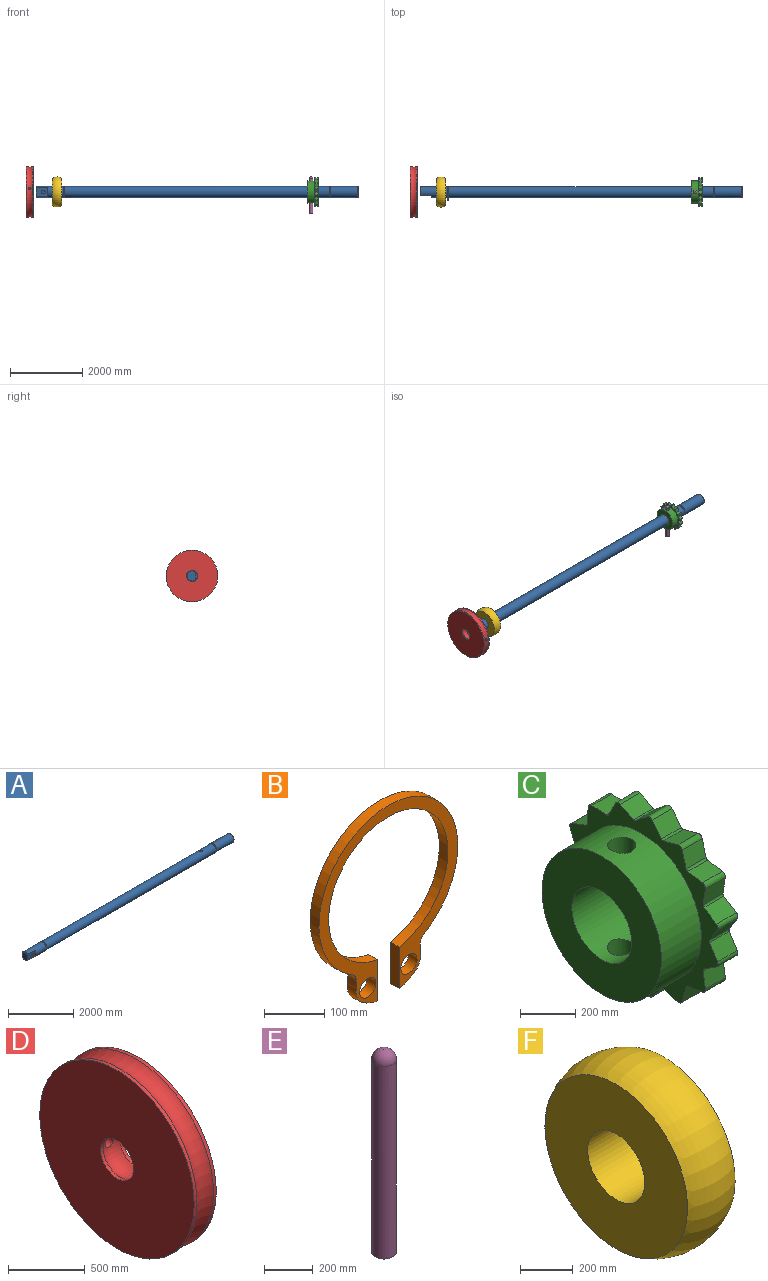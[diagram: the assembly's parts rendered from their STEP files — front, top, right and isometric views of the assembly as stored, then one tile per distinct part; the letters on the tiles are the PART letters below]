
ASSEMBLY  parts=6 mates=6
PART A: 18 faces, bbox 8890x304.8x304.8 mm
  f0: plane 279.4x241.3mm, normal (-1,0,0), area 56290.2mm2, adj f2,f15
  f1: cylinder r=152.4mm len=749.3mm, axis (-1,0,0), area 639360mm2, adj f2,f11,f14,f15
  f2: cone r=139.7mm half-angle=45deg, axis (1,0,0), area 12278.4mm2, adj f0,f1,f15
  f3: plane 279.4x279.4mm, normal (1,0,0), area 61311.6mm2, adj f12
  f4: cylinder r=152.4mm len=749.3mm, axis (-1,0,0), area 717497.8mm2, adj f5,f12
  f5: plane 304.8x304.8mm, normal (-1,0,0), area 31922.6mm2, adj f4,f6
  f6: cylinder r=114.3mm len=228.6mm, axis (-1,0,0), area 18241.5mm2, adj f5,f7
  f7: plane 304.8x304.8mm, normal (1,0,0), area 31922.6mm2, adj f6,f8
  f8: cylinder r=152.4mm len=7315.2mm, axis (-1,0,0), area 6988289.9mm2, adj f7,f9,f13
  f9: plane 304.8x304.8mm, normal (-1,0,0), area 31922.6mm2, adj f8,f10
  f10: cylinder r=114.3mm len=228.6mm, axis (-1,0,0), area 18241.5mm2, adj f9,f11
  f11: plane 304.8x304.8mm, normal (1,0,0), area 31922.6mm2, adj f1,f10
  f12: cone r=152.4mm half-angle=45deg, axis (-1,0,0), area 16481.6mm2, adj f3,f4
  f13: cylinder r=50.8mm len=304.8mm, axis (0,0,1), area 94524.2mm2, adj f8
  f14: plane 227.18x50.8mm, normal (-1,0,0), area 7993.5mm2, adj f1,f15
  f15: plane 317.5x227.19mm, normal (0,-1,0), area 63801.9mm2, adj f0,f1,f2,f14,f16
  f16: cylinder r=50.8mm len=101.6mm, axis (0,1,0), area 8107.3mm2, adj f15,f17
  f17: plane 101.6x101.6mm, normal (0,-1,0), area 8107.3mm2, adj f16
PART B: 16 faces, bbox 325.1x20.3x383.8 mm
  f0: cylinder r=20.32mm len=20.32mm, axis (0,1,0), area 404.6mm2, adj f1,f12,f14,f15
  f1: plane 20.32x12.7mm, normal (-1,0,0), area 258.1mm2, adj f0,f2,f14,f15
  f2: cylinder r=38.1mm len=33.8mm, axis (0,1,0), area 737.9mm2, adj f1,f3,f14,f15
  f3: cylinder r=88.9mm len=40.51mm, axis (0,1,0), area 915mm2, adj f2,f4,f14,f15
  f4: plane 83.82x20.32mm, normal (1,0,0), area 1703.2mm2, adj f3,f5,f14,f15
  f5: cylinder r=139.7mm len=279.4mm, axis (0,1,0), area 16798.1mm2, adj f4,f6,f14,f15
  f6: plane 83.82x20.32mm, normal (-1,0,0), area 1703.2mm2, adj f5,f7,f14,f15
  f7: cylinder r=88.9mm len=40.51mm, axis (0,1,0), area 915mm2, adj f6,f8,f14,f15
  f8: cylinder r=38.1mm len=33.8mm, axis (0,1,0), area 737.9mm2, adj f7,f9,f14,f15
  f9: plane 20.32x12.7mm, normal (1,0,0), area 258.1mm2, adj f8,f10,f14,f15
  f10: cylinder r=20.32mm len=20.32mm, axis (0,1,0), area 404.6mm2, adj f9,f12,f14,f15
  f11: cylinder r=19.05mm len=38.1mm, axis (0,1,0), area 2432.2mm2, adj f14,f15
  f12: cylinder r=162.56mm len=325.12mm, axis (0,1,0), area 17175.7mm2, adj f0,f10,f14,f15
  f13: cylinder r=19.05mm len=38.1mm, axis (0,1,0), area 2432.2mm2, adj f14,f15
  f14: plane 383.75x325.12mm, normal (0,-1,0), area 23940.7mm2, adj f0,f1,f2,f3,f4,f5,f6,f7
  f15: plane 383.75x325.12mm, normal (0,1,0), area 23940.7mm2, adj f0,f1,f2,f3,f4,f5,f6,f7
PART C: 67 faces, bbox 304.8x789.2x793.3 mm
  f0: plane 609.6x609.6mm, normal (-1,0,0), area 218897.6mm2, adj f1,f4
  f1: cylinder r=152.4mm len=304.8mm, axis (-1,0,0), area 275429.2mm2, adj f0,f2,f5,f6
  f2: plane 793.34x789.19mm, normal (1,0,0), area 359950.9mm2, adj f1,f7,f8,f9,f10,f11,f12,f13
  f3: plane 793.34x789.19mm, normal (-1,0,0), area 141053.3mm2, adj f4,f7,f8,f9,f10,f11,f12,f13
  f4: cylinder r=304.8mm len=609.6mm, axis (-1,0,0), area 372930.5mm2, adj f0,f3,f5,f6
  f5: cylinder r=50.8mm len=161.12mm, axis (0,0,1), area 49346.9mm2, adj f1,f4
  f6: cylinder r=50.8mm len=161.12mm, axis (0,0,1), area 49345.3mm2, adj f1,f4
  f7: plane 101.6x73.6mm, normal (0,0.26,0.97), area 7741.9mm2, adj f2,f3,f8,f66
  f8: cylinder r=10.07mm len=101.6mm, axis (1,0,0), area 1178.2mm2, adj f2,f3,f7,f9
  f9: plane 101.6x59.22mm, normal (0,-0.78,0.63), area 7741.9mm2, adj f2,f3,f8,f10
  f10: cylinder r=17.96mm len=101.6mm, axis (1,0,0), area 2866.4mm2, adj f2,f3,f9,f11
  f11: plane 101.6x59.22mm, normal (0,0.63,0.78), area 7741.9mm2, adj f2,f3,f10,f12
  f12: cylinder r=10.07mm len=101.6mm, axis (1,0,0), area 1178.2mm2, adj f2,f3,f11,f13
  f13: plane 101.6x67.89mm, normal (0,-0.45,0.89), area 7741.9mm2, adj f2,f3,f12,f14
  f14: cylinder r=17.96mm len=101.6mm, axis (1,0,0), area 2866.4mm2, adj f2,f3,f13,f15
  f15: plane 101.6x67.89mm, normal (0,0.89,0.45), area 7741.9mm2, adj f2,f3,f14,f16
  f16: cylinder r=10.07mm len=101.6mm, axis (1,0,0), area 1178.2mm2, adj f2,f3,f15,f17
  f17: plane 101.6x76.1mm, normal (0,-0.05,1), area 7741.9mm2, adj f2,f3,f16,f18
  f18: cylinder r=17.96mm len=101.6mm, axis (1,0,0), area 2866.4mm2, adj f2,f3,f17,f19
  f19: plane 101.6x76.1mm, normal (0,1,0.05), area 7741.9mm2, adj f2,f3,f18,f20
  f20: cylinder r=10.07mm len=101.6mm, axis (1,0,0), area 1178.2mm2, adj f2,f3,f19,f21
  f21: plane 101.6x71.14mm, normal (0,0.36,0.93), area 7741.9mm2, adj f2,f3,f20,f22
  f22: cylinder r=17.96mm len=101.6mm, axis (1,0,0), area 2866.4mm2, adj f2,f3,f21,f23
  f23: plane 101.6x71.14mm, normal (0,0.93,-0.36), area 7741.9mm2, adj f2,f3,f22,f24
  f24: cylinder r=10.07mm len=101.6mm, axis (1,0,0), area 1178.2mm2, adj f2,f3,f23,f25
  f25: plane 101.6x53.88mm, normal (0,0.71,0.71), area 7741.9mm2, adj f2,f3,f24,f26
  f26: cylinder r=17.96mm len=101.6mm, axis (1,0,0), area 2866.4mm2, adj f2,f3,f25,f27
  f27: plane 101.6x53.88mm, normal (0,0.71,-0.71), area 7741.9mm2, adj f2,f3,f26,f28
  f28: cylinder r=10.07mm len=101.6mm, axis (1,0,0), area 1178.2mm2, adj f2,f3,f27,f29
  f29: plane 101.6x71.14mm, normal (0,0.93,0.36), area 7741.9mm2, adj f2,f3,f28,f30
  f30: cylinder r=17.96mm len=101.6mm, axis (1,0,0), area 2866.4mm2, adj f2,f3,f29,f31
  f31: plane 101.6x71.14mm, normal (0,0.36,-0.93), area 7741.9mm2, adj f2,f3,f30,f32
  f32: cylinder r=10.07mm len=101.6mm, axis (1,0,0), area 1178.2mm2, adj f2,f3,f31,f33
  f33: plane 101.6x76.1mm, normal (0,1,-0.05), area 7741.9mm2, adj f2,f3,f32,f34
  f34: cylinder r=17.96mm len=101.6mm, axis (1,0,0), area 2866.4mm2, adj f2,f3,f33,f35
  f35: plane 101.6x76.1mm, normal (0,-0.05,-1), area 7741.9mm2, adj f2,f3,f34,f36
  f36: cylinder r=10.07mm len=101.6mm, axis (1,0,0), area 1178.2mm2, adj f2,f3,f35,f37
  f37: plane 101.6x67.89mm, normal (0,0.89,-0.45), area 7741.9mm2, adj f2,f3,f36,f38
  f38: cylinder r=17.96mm len=101.6mm, axis (1,0,0), area 2866.4mm2, adj f2,f3,f37,f39
  f39: plane 101.6x67.89mm, normal (0,-0.45,-0.89), area 7741.9mm2, adj f2,f3,f38,f40
  f40: cylinder r=10.07mm len=101.6mm, axis (1,0,0), area 1178.2mm2, adj f2,f3,f39,f41
  f41: plane 101.6x59.22mm, normal (0,0.63,-0.78), area 7741.9mm2, adj f2,f3,f40,f42
  f42: cylinder r=17.96mm len=101.6mm, axis (1,0,0), area 2866.4mm2, adj f2,f3,f41,f43
  f43: plane 101.6x59.22mm, normal (0,-0.78,-0.63), area 7741.9mm2, adj f2,f3,f42,f44
  f44: cylinder r=10.07mm len=101.6mm, axis (1,0,0), area 1178.2mm2, adj f2,f3,f43,f45
  f45: plane 101.6x73.6mm, normal (0,0.26,-0.97), area 7741.9mm2, adj f2,f3,f44,f46
  f46: cylinder r=17.96mm len=101.6mm, axis (1,0,0), area 2866.4mm2, adj f2,f3,f45,f47
  f47: plane 101.6x73.6mm, normal (0,-0.97,-0.26), area 7741.9mm2, adj f2,f3,f46,f48
  f48: cylinder r=10.07mm len=101.6mm, axis (1,0,0), area 1178.2mm2, adj f2,f3,f47,f49
  f49: plane 101.6x75.26mm, normal (0,-0.16,-0.99), area 7741.9mm2, adj f2,f3,f48,f50
  f50: cylinder r=17.96mm len=101.6mm, axis (1,0,0), area 2866.4mm2, adj f2,f3,f49,f51
  f51: plane 101.6x75.26mm, normal (0,-0.99,0.16), area 7741.9mm2, adj f2,f3,f50,f52
  f52: cylinder r=10.07mm len=101.6mm, axis (1,0,0), area 1178.2mm2, adj f2,f3,f51,f53
  f53: plane 101.6x63.91mm, normal (0,-0.54,-0.84), area 7741.9mm2, adj f2,f3,f52,f54
  f54: cylinder r=17.96mm len=101.6mm, axis (1,0,0), area 2866.4mm2, adj f2,f3,f53,f55
  f55: plane 101.6x63.91mm, normal (0,-0.84,0.54), area 7741.9mm2, adj f2,f3,f54,f56
  f56: cylinder r=10.07mm len=101.6mm, axis (1,0,0), area 1178.2mm2, adj f2,f3,f55,f57
  f57: plane 101.6x63.91mm, normal (0,-0.84,-0.54), area 7741.9mm2, adj f2,f3,f56,f58
  f58: cylinder r=17.96mm len=101.6mm, axis (1,0,0), area 2866.4mm2, adj f2,f3,f57,f59
  f59: plane 101.6x63.91mm, normal (0,-0.54,0.84), area 7741.9mm2, adj f2,f3,f58,f60
  f60: cylinder r=10.07mm len=101.6mm, axis (1,0,0), area 1178.2mm2, adj f2,f3,f59,f61
  f61: plane 101.6x75.26mm, normal (0,-0.99,-0.16), area 7741.9mm2, adj f2,f3,f60,f62
  f62: cylinder r=17.96mm len=101.6mm, axis (1,0,0), area 2866.4mm2, adj f2,f3,f61,f63
  f63: plane 101.6x75.26mm, normal (0,-0.16,0.99), area 7741.9mm2, adj f2,f3,f62,f64
  f64: cylinder r=10.07mm len=101.6mm, axis (1,0,0), area 1178.2mm2, adj f2,f3,f63,f65
  f65: plane 101.6x73.6mm, normal (0,-0.97,0.26), area 7741.9mm2, adj f2,f3,f64,f66
  f66: cylinder r=17.96mm len=101.6mm, axis (1,0,0), area 2866.4mm2, adj f2,f3,f7,f65
PART D: 9 faces, bbox 203.2x1564.3x1564.3 mm
  f0: torus R=50.8mm, axis (-1,0,0), area 169130.2mm2, adj f1,f7,f8
  f1: cylinder r=152.4mm len=304.8mm, axis (-1,0,0), area 24322mm2, adj f0,f2
  f2: plane 1422.4x1422.4mm, normal (1,0,0), area 1516068.8mm2, adj f1,f3
  f3: cylinder r=711.2mm len=1422.4mm, axis (-1,0,0), area 113502.5mm2, adj f2,f4
  f4: torus R=812.8mm, axis (-1,0,0), area 708556.6mm2, adj f3,f5,f8
  f5: cylinder r=711.2mm len=1422.4mm, axis (-1,0,0), area 113502.5mm2, adj f4,f6
  f6: plane 1422.4x1422.4mm, normal (-1,0,0), area 1516068.8mm2, adj f5,f7
  f7: cylinder r=152.4mm len=304.8mm, axis (-1,0,0), area 24322mm2, adj f0,f6
  f8: cylinder r=38.1mm len=519.7mm, axis (0,-1,0), area 123373.9mm2, adj f0,f4
PART E: 3 faces, bbox 101.6x101.6x1016 mm
  f0: cylinder r=50.8mm len=965.2mm, axis (0,0,-1), area 308078.1mm2, adj f1,f2
  f1: plane 101.6x101.6mm, normal (0,0,-1), area 8107.3mm2, adj f0
  f2: sphere r=50.8mm, area 16214.6mm2, adj f0
PART F: 4 faces, bbox 254x762x796 mm
  f0: plane 762x762mm, normal (-1,0,0), area 383070.9mm2, adj f1,f3
  f1: cylinder r=152.4mm len=304.8mm, axis (-1,0,0), area 243219.6mm2, adj f0,f2
  f2: plane 762x762mm, normal (1,0,0), area 383070.9mm2, adj f1,f3
  f3: torus R=161.03mm, axis (-1,0,0), area 674487.1mm2, adj f0,f2
PLACE A at identity fixed
PLACE B rot(axis=(-0.58,0.58,0.58),120deg) t=(-3675.95,0,0)mm
PLACE C t=(3048,0,0)mm
PLACE D rot(axis=(1,0,0),171.8deg) t=(-4620.5,0,0)mm
PLACE E t=(3149.6,0,-591.66)mm
PLACE F rot(axis=(-1,0,0),26.9deg) t=(-3868.57,0,0)mm
MATE slider E.f0 <-> A.f13  axis (0,0,-1) through (3149.6,0,-109.06)mm
MATE cylindrical D.f0 <-> A.f1  axis (-1,0,0) through (-4544.3,0,0)mm
MATE slider E.f0 <-> C.f5  axis (0,0,-1) through (3149.6,0,-109.06)mm
MATE slider C.f1 <-> A.f1  axis (-1,0,0) through (3200.4,0,0)mm
MATE slider B.f12 <-> A.f1  axis (1,0,0) through (-3655.63,0,0)mm
MATE cylindrical F.f1 <-> A.f1  axis (-1,0,0) through (-3741.57,0,0)mm
